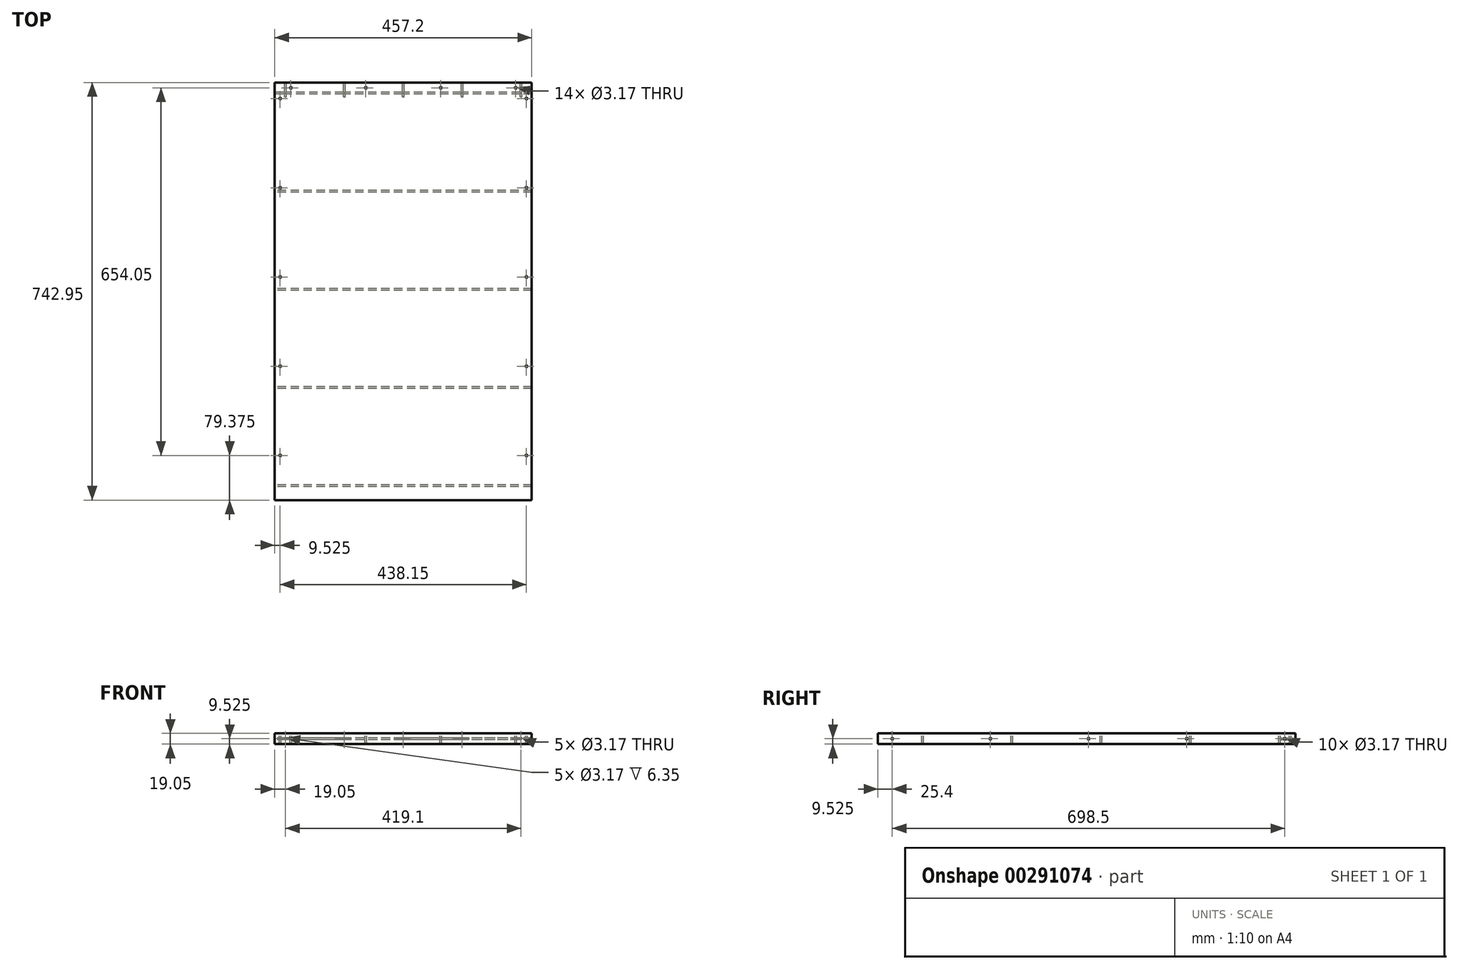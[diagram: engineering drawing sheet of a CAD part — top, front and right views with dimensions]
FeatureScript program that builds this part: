
annotation { "Feature Type Name" : "Feature", "Feature Type Description" : "" }
export const myFeature = defineFeature(function(context is Context, id is Id, definition is map)
    precondition{}
    {
        {
            var Q0;
            Q0=qCreatedBy(makeId("Top.planeOp"),FACE);
            var sketch = newSketch(context, id + "F0", { "sketchPlane" : qUnion([Q0])});
            skLineSegment(sketch, "E0.bottom", {"start": v(0, 0) * mm, "end": v(457.2, 0) * mm});
            skLineSegment(sketch, "E0.top", {"start": v(0, -742.95) * mm, "end": v(457.2, -742.95) * mm});
            skLineSegment(sketch, "E0.left", {"start": v(0, 0) * mm, "end": v(0, -742.95) * mm});
            skLineSegment(sketch, "E0.right", {"start": v(457.2, 0) * mm, "end": v(457.2, -742.95) * mm});
            skSolve(sketch);
        }
        {
            var Q0;
            Q0 = qSketchRegion(id + "F0", true);
            extrude(context, id + "F1", {"entities" : qUnion([Q0]), "oppositeDirection" : true, "depth" : 19.05 * mm});
        }
        {
            var Q0;
            Q0=qCreatedBy(makeId("Top.planeOp"),FACE);
            var sketch = newSketch(context, id + "F2", { "sketchPlane" : qUnion([Q0])});
            skCircle(sketch, "E1", {"center": v(9.53, -28.58) * mm, "radius": 1.59 * mm});
            skCircle(sketch, "E2.0.1.0", {"center": v(9.53, -187.33) * mm, "radius": 1.59 * mm});
            skCircle(sketch, "E2.0.2.0", {"center": v(9.53, -346.08) * mm, "radius": 1.59 * mm});
            skCircle(sketch, "E2.0.3.0", {"center": v(9.53, -504.82) * mm, "radius": 1.59 * mm});
            skCircle(sketch, "E2.0.4.0", {"center": v(9.53, -663.58) * mm, "radius": 1.59 * mm});
            skCircle(sketch, "E2.1.0.0", {"center": v(447.68, -28.58) * mm, "radius": 1.59 * mm});
            skCircle(sketch, "E2.1.1.0", {"center": v(447.68, -187.33) * mm, "radius": 1.59 * mm});
            skCircle(sketch, "E2.1.2.0", {"center": v(447.68, -346.08) * mm, "radius": 1.59 * mm});
            skCircle(sketch, "E2.1.3.0", {"center": v(447.68, -504.82) * mm, "radius": 1.59 * mm});
            skCircle(sketch, "E2.1.4.0", {"center": v(447.68, -663.58) * mm, "radius": 1.59 * mm});
            skLineSegment(sketch, "E2.direction1", {"start": v(9.53, -28.58) * mm, "end": v(447.68, -28.58) * mm, "construction": true});
            skLineSegment(sketch, "E2.direction2", {"start": v(9.53, -28.58) * mm, "end": v(9.53, -187.33) * mm, "construction": true});
            skSolve(sketch);
        }
        {
            var Q0;
            Q0 = qSketchRegion(id + "F2", true);
            extrude(context, id + "F3", {"entities" : qUnion([Q0]), "operationType" : NewBodyOperationType.REMOVE, "endBound" : BoundingType.THROUGH_ALL, "oppositeDirection" : true, "depth" : 25.4 * mm});
        }
        {
            var Q0;
            Q0=qCreatedBy(makeId("Top.planeOp"),FACE);
            var sketch = newSketch(context, id + "F4", { "sketchPlane" : qUnion([Q0])});
            skCircle(sketch, "E3", {"center": v(28.58, -9.52) * mm, "radius": 1.59 * mm});
            skCircle(sketch, "E4.1.0.0", {"center": v(161.93, -9.52) * mm, "radius": 1.59 * mm});
            skCircle(sketch, "E4.2.0.0", {"center": v(295.28, -9.52) * mm, "radius": 1.59 * mm});
            skCircle(sketch, "E4.3.0.0", {"center": v(428.63, -9.52) * mm, "radius": 1.59 * mm});
            skLineSegment(sketch, "E4.direction1", {"start": v(28.58, -9.52) * mm, "end": v(161.93, -9.52) * mm, "construction": true});
            skSolve(sketch);
        }
        {
            var Q0;
            Q0 = qSketchRegion(id + "F4", true);
            extrude(context, id + "F5", {"entities" : qUnion([Q0]), "operationType" : NewBodyOperationType.REMOVE, "endBound" : BoundingType.THROUGH_ALL, "oppositeDirection" : true, "depth" : 25.4 * mm});
        }
        {
            var Q0;
            Q0=qCreatedBy(makeId("Right.planeOp"),FACE);
            var sketch = newSketch(context, id + "F6", { "sketchPlane" : qUnion([Q0])});
            skCircle(sketch, "E5", {"center": v(-19.05, -9.53) * mm, "radius": 1.59 * mm});
            skCircle(sketch, "E6.1.0.0", {"center": v(-193.68, -9.53) * mm, "radius": 1.59 * mm});
            skCircle(sketch, "E6.2.0.0", {"center": v(-368.3, -9.53) * mm, "radius": 1.59 * mm});
            skCircle(sketch, "E6.3.0.0", {"center": v(-542.93, -9.53) * mm, "radius": 1.59 * mm});
            skCircle(sketch, "E6.4.0.0", {"center": v(-717.55, -9.53) * mm, "radius": 1.59 * mm});
            skLineSegment(sketch, "E6.direction1", {"start": v(-19.05, -9.53) * mm, "end": v(-193.68, -9.52) * mm, "construction": true});
            skSolve(sketch);
        }
        {
            var Q0;
            Q0 = qSketchRegion(id + "F6", true);
            extrude(context, id + "F7", {"entities" : qUnion([Q0]), "operationType" : NewBodyOperationType.REMOVE, "endBound" : BoundingType.THROUGH_ALL, "depth" : 25.4 * mm});
        }
        {
            var Q0;
            Q0=qCreatedBy(makeId("Front.planeOp"),FACE);
            var sketch = newSketch(context, id + "F8", { "sketchPlane" : qUnion([Q0])});
            skCircle(sketch, "E7", {"center": v(19.05, -9.53) * mm, "radius": 1.59 * mm});
            skCircle(sketch, "E8.1.0.0", {"center": v(123.83, -9.53) * mm, "radius": 1.59 * mm});
            skCircle(sketch, "E8.2.0.0", {"center": v(228.6, -9.53) * mm, "radius": 1.59 * mm});
            skCircle(sketch, "E8.3.0.0", {"center": v(333.38, -9.53) * mm, "radius": 1.59 * mm});
            skCircle(sketch, "E8.4.0.0", {"center": v(438.15, -9.53) * mm, "radius": 1.59 * mm});
            skLineSegment(sketch, "E8.direction1", {"start": v(19.05, -9.53) * mm, "end": v(123.83, -9.53) * mm, "construction": true});
            skSolve(sketch);
        }
        {
            var Q0;
            Q0 = qSketchRegion(id + "F8", true);
            extrude(context, id + "F9", {"entities" : qUnion([Q0]), "operationType" : NewBodyOperationType.REMOVE, "depth" : 25.4 * mm});
        }
    });
